# Revit family: SALI-GPS150xWSxx
name_source: partatom
category: Leuchten
units: mm (PartAtom-declared; Revit-internal decimal feet)

## family parameters
Basisbauteil = Fläche
Beim Laden mit Abzugskörper schneiden = Nein
Bemaßung runder Anschluss = Durchmesser verwenden
Gemeinsam genutzt = Nein
Lichtquelle = Ja
OmniClass-Nummer = 23.80.70.11
OmniClass-Titel = Luminaries for Internal Lighting
Raumberechnungspunkt = Nein
Teiletyp = Normal

## types (4) — shared parameters
Baugruppenkennzeichen = D5020200
Emissionsform beim Rendern sichtbar = Nein
Farbfilter = 16777215
Farbtemperaturverschiebung bei Dämpfen der Lampe = <Keine Auswahl>
Hersteller = RIDI Leuchten GmbH
Lampe = LED
Neigungswinkel = 90.00°
URL = www.ridi.de
Von Breite des Rechtecks ausssenden = 1479 mm  [stored 4.85236 ft]
Von Länge des Rechtecks aussenden = 61 mm  [stored 0.200131 ft]
brand = RIDI
conformity mark = CE
electrical safety class = 1
height = 62 mm  [stored 0.203412 ft]
ingress protection (IP) code = IP54
length = 1504 mm  [stored 4.93438 ft]
nominal frequency = 50-60Hz
nominal voltage = 230
voltage type (AC, DC, UC) = AC
weight = 3kg
width = 67 mm
zero-valued in all types: Vorgabe-Ansicht

## per-type parameters (varying)
| type | Datei für fotometrisches Netz | Modell | Scheinlast | rated input power |
| SALI-GPS150-FLWS840B0900 | Master_VL1GP1486-5RFWS840B0900.IES | 1552022 | 57 VA | 57 |
| SALI-GPS150-FLWS840E0900 | Master_VL1GP1486-5RFWS840E0900.IES | 1552023 | 57 VA | 57 |
| SALI-GPS150-DAWS840B0900 | Master_VL1GP1486-5RFWS840B0900.IES | 1562022 | 58 VA | 58 |
| SALI-GPS150-DAWS840E0900 | Master_VL1GP1486-5RFWS840E0900.IES | 1562023 | 58 VA | 58 |

note: column(s) folded — value = type name in every type: product name

note: [stored X ft] marks values corroborated as IEEE doubles in the binary element streams (Revit-internal decimal feet)
